# Revit family: НЕВАТОМ_Шумоглушитель ГП, Версия 2
name_source: partatom
category: Арматура воздуховодов
revit_build: Autodesk Revit 2017 (Build: 20170118_1100(x64)
units: mm (PartAtom-declared; Revit-internal decimal feet)

## family parameters
Всегда вертикально = Нет
На основе рабочей плоскости = Нет
Общий = Нет
При загрузке вырезать с полостями = Нет
Размер круглого соединителя = Использовать диаметр
Тип детали = Вставляется

## types (26) — shared parameters
100 = 100 мм
A1 = 200 мм
ADSK_Единица измерения = шт
ADSK_Завод-изготовитель = НЕВАТОМ
ADSK_Количество = 1
ADSK_Материал наименование = Оцинкованная сталь
ADSK_Наименование = Глушитель ГП
ADSK_Потеря давления воздуха = 0.0 Па
ADSK_Расход воздуха = 0.0 м³/ч
Nevatom_URL = https://t.me
t = 2 мм
Материал = Сталь оцинкованная
zero-valued in all types: ADSK_Масса

## per-type parameters (varying)
| type | A | ADSK_Марка | ADSK_Размер_Высота | ADSK_Размер_Длина | ADSK_Размер_Ширина | B | L | T | Количество кассет |
| 800x500–1000 | 800 мм | ГП-800x500–1000–200/2 | 500 мм | 800 мм | 1000 мм | 500 мм | 1000 мм | 30 мм | 2 |
| 1200x500-1000 | 1200 мм | ГП-1200x500–1000–200/3 | 500 мм | 1200 мм | 1000 мм | 500 мм | 1000 мм | 30 мм | 3 |
| 1600x500–1000 | 1600 мм | ГП-1600x500–1000–200/4 | 500 мм | 1600 мм | 1000 мм | 500 мм | 1000 мм | 30 мм | 4 |
| 800x1000–1000 | 800 мм | ГП-800x1000–1000–200/2 | 1000 мм | 800 мм | 1000 мм | 1000 мм | 1000 мм | 30 мм | 2 |
| 1200x1000–1000 | 1200 мм | ГП-1200x1000–1000–200/3 | 1000 мм | 1200 мм | 1000 мм | 1000 мм | 1000 мм | 30 мм | 3 |
| 1600x1000–1000 | 1600 мм | ГП-1600x1000–1000–200/3 | 1000 мм | 1600 мм | 1000 мм | 1000 мм | 1000 мм | 30 мм | 4 |
| 2000x1000–1000 | 2000 мм | ГП-2000x1000–1000–200/5 | 1000 мм | 2000 мм | 1000 мм | 1000 мм | 1000 мм | 32 мм | 5 |
| 800x1500–1000 | 800 мм | ГП-800x1500–1000–200/2 | 1500 мм | 800 мм | 1000 мм | 1500 мм | 1000 мм | 30 мм | 2 |
| 1200x1500–1000 | 1200 мм | ГП-1200x1500–1000–200/3 | 1500 мм | 1200 мм | 1000 мм | 1500 мм | 1000 мм | 30 мм | 3 |
| 1600x1500–1000 | 1600 мм | ГП-1600x1500–1000–200/4 | 1500 мм | 1600 мм | 1000 мм | 1500 мм | 1000 мм | 32 мм | 4 |
| 800x2000–1000 | 800 мм | ГП-800x2000–1000–200/2 | 2000 мм | 800 мм | 1000 мм | 2000 мм | 1000 мм | 30 мм | 2 |
| 1200x2000–1000 | 1200 мм | ГП-1200x2000–1000–200/3 | 2000 мм | 1200 мм | 1000 мм | 2000 мм | 1000 мм | 32 мм | 3 |
| 1600x2000–1000 | 1600 мм | ГП-1600x2000–1000–200/4 | 2000 мм | 1600 мм | 1000 мм | 2000 мм | 1000 мм | 32 мм | 4 |
| 800x500–1500 | 800 мм | ГП-800x500–1500–200/2 | 500 мм | 800 мм | 1500 мм | 500 мм | 1500 мм | 30 мм | 2 |
| 1200x500–1500 | 1200 мм | ГП-1200x500–1500–200/3 | 500 мм | 1200 мм | 1500 мм | 500 мм | 1500 мм | 30 мм | 3 |
| 1600x500–1500 | 1600 мм | ГП-1600x500–1500–200/4 | 500 мм | 1600 мм | 1500 мм | 500 мм | 1500 мм | 30 мм | 4 |
| 800x1000–1500 | 800 мм | ГП-800x1000–1500–200/2 | 1000 мм | 800 мм | 1500 мм | 1000 мм | 1500 мм | 30 мм | 2 |
| 1200x1000–1500 | 1200 мм | ГП-1200x1000–1500–200/3 | 1000 мм | 1200 мм | 1500 мм | 1000 мм | 1500 мм | 30 мм | 3 |
| 1600x1000–1500 | 1600 мм | ГП-1600x1000–1500–200/4 | 1000 мм | 1600 мм | 1500 мм | 1000 мм | 1500 мм | 30 мм | 4 |
| 2000x1000–1500 | 2000 мм | ГП-2000x1000–1500–200/5 | 1000 мм | 2000 мм | 1500 мм | 1000 мм | 1500 мм | 32 мм | 5 |
| 800x1500–1500 | 800 мм | ГП-800x1500–1500–200/2 | 1500 мм | 800 мм | 1500 мм | 1500 мм | 1500 мм | 30 мм | 2 |
| 1200x1500–1500 | 1200 мм | ГП-1200x1500–1500–200/3 | 1500 мм | 1200 мм | 1500 мм | 1500 мм | 1500 мм | 30 мм | 3 |
| 1600x1500–1500 | 1600 мм | ГП-1600x1500–1500–200/3 | 1500 мм | 1600 мм | 1500 мм | 1500 мм | 1500 мм | 32 мм | 4 |
| 800x2000–1500 | 800 мм | ГП-800x2000–1500–200/2 | 2000 мм | 800 мм | 1500 мм | 2000 мм | 1500 мм | 30 мм | 2 |
| 1200x2000–1500 | 1200 мм | ГП-1200x2000–1500–200/3 | 2000 мм | 1200 мм | 1500 мм | 2000 мм | 1500 мм | 32 мм | 3 |
| 1600x2000–1500 | 1600 мм | 1600x2000–1500–200/4 | 2000 мм | 1600 мм | 1500 мм | 2000 мм | 1500 мм | 32 мм | 4 |
